# Revit family: LeL Tago 4.0
name_source: partatom
category: Lighting Fixtures
units: mm (PartAtom-declared; Revit-internal decimal feet)

## family parameters
Cut with Voids When Loaded = Yes
Host = Face
Light Source = No
Part Type = Normal
Room Calculation Point = No
Round Connector Dimension = Use Diameter
Shared = No

## types (3) — shared parameters
Accessories = WCTG10A0T outer casing
Alimentazione = 48 V
Apparent Load = 14 VA
CCT = 4000 K
CRI = 80
Default Elevation = 1219 mm
Description = Outdoor Linear Profile
Finish = LeL Black
IK = IK09
IP = IP65 IP67 IP69
Lamp = LED
Lenght = 270 mm  [stored 0.885827 ft]
Manufacturer = L&L Luce&Light
Model = TG40
Outercasing = 310 mm
Rated Power supply = 48 V
URL = https://www.lucelight.it
Wattage = 14 W
Weight = 2.20 kg

## per-type parameters (varying)
| type | Optic |
| 4.0 L 52° 14W | TAGO Light source : 4.0 L 52° 14W 48Vdc |
| 4.0 M 30° 14W | TAGO Light source : 4.0 M 30° 14W 48Vdc |
| 4.0 S 24° 14W | TAGO Light source : 4.0 S 24° 14W 48Vdc |

note: [stored X ft] marks values corroborated as IEEE doubles in the binary element streams (Revit-internal decimal feet)

## geometry (parser evidence)
native form markers: Sweep x3
no freeform markers — native parametric forms only
